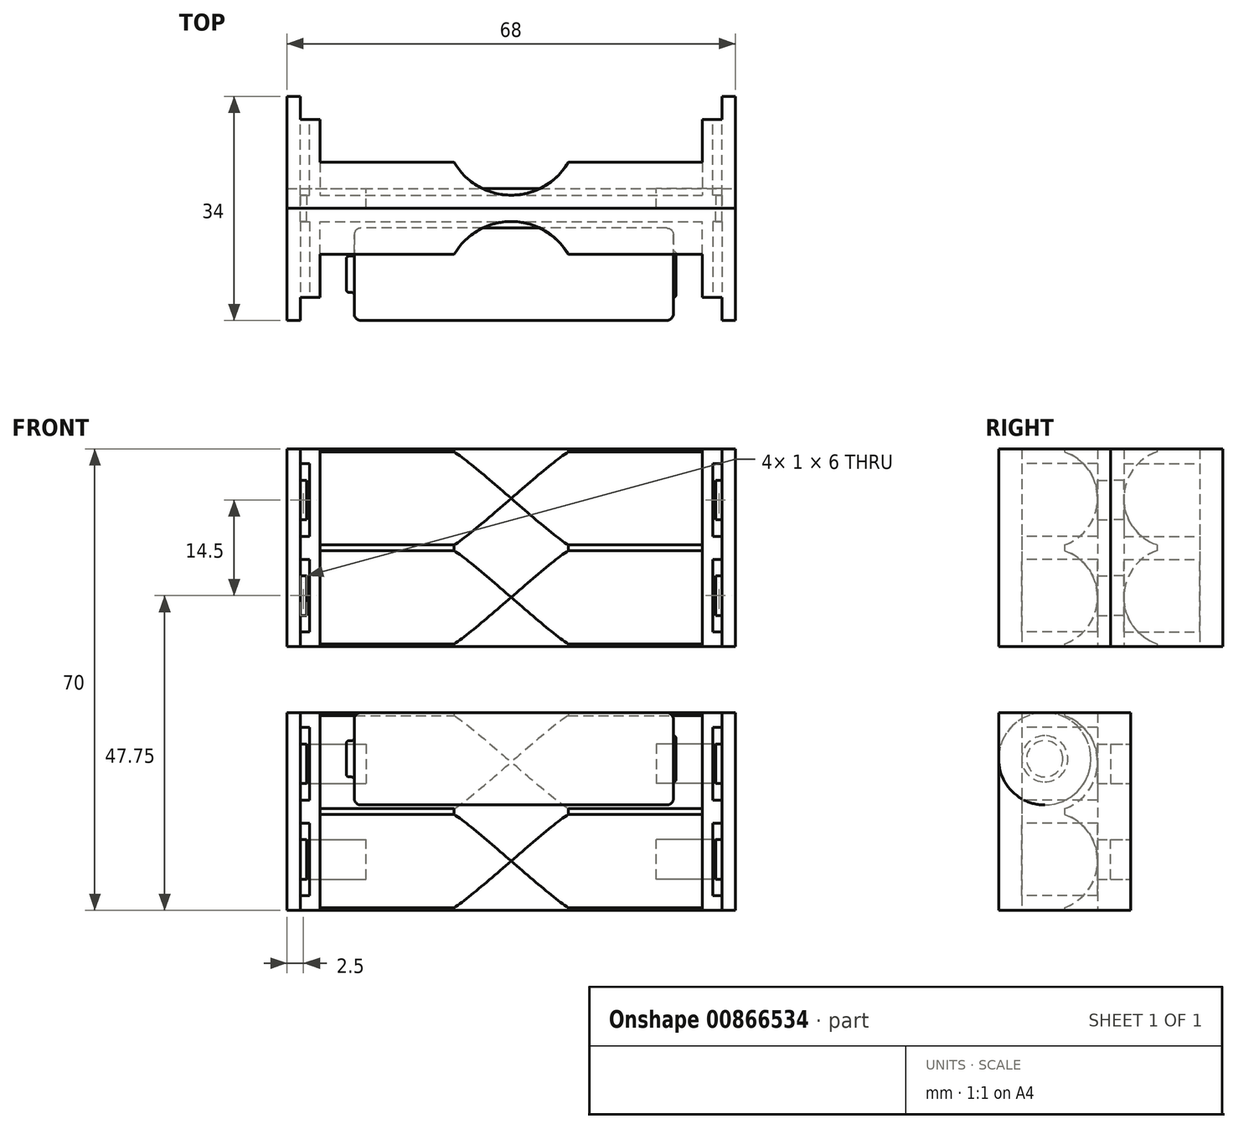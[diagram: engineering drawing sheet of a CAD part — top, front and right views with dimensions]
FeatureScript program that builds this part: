
annotation { "Feature Type Name" : "Feature", "Feature Type Description" : "" }
export const myFeature = defineFeature(function(context is Context, id is Id, definition is map)
    precondition{}
    {
        {
            var Q0;
            Q0=qCreatedBy(makeId("Top.planeOp"),FACE);
            var sketch = newSketch(context, id + "F0", { "sketchPlane" : qUnion([Q0])});
            skLineSegment(sketch, "E0.bottom", {"start": v(-34, 10) * mm, "end": v(34, 10) * mm});
            skLineSegment(sketch, "E0.top", {"start": v(-34, -10) * mm, "end": v(-32, -10) * mm});
            skLineSegment(sketch, "E0.left", {"start": v(-34, 10) * mm, "end": v(-34, -10) * mm});
            skLineSegment(sketch, "E0.right", {"start": v(34, 10) * mm, "end": v(34, -10) * mm});
            skLineSegment(sketch, "E1", {"start": v(0, 0) * mm, "end": v(0, 13.76) * mm, "construction": true});
            skArc(sketch, "E2", {"start": v(8.66, 0) * mm, "mid": v(0, 5) * mm, "end": v(-8.66, 0) * mm});
            skLineSegment(sketch, "E3", {"start": v(-32, -10) * mm, "end": v(-32, -6.5) * mm});
            skLineSegment(sketch, "E4", {"start": v(-32, -6.5) * mm, "end": v(-29, -6.5) * mm});
            skLineSegment(sketch, "E5", {"start": v(-29, -6.5) * mm, "end": v(-29, 0) * mm});
            skLineSegment(sketch, "E6", {"start": v(-29, 0) * mm, "end": v(-8.66, 0) * mm});
            skLineSegment(sketch, "E7", {"start": v(29, 0) * mm, "end": v(29, -6.5) * mm});
            skLineSegment(sketch, "E8", {"start": v(29, -6.5) * mm, "end": v(32, -6.5) * mm});
            skLineSegment(sketch, "E9", {"start": v(32, -6.5) * mm, "end": v(32, -10) * mm});
            skLineSegment(sketch, "E10.trimOffspring", {"start": v(32, -10) * mm, "end": v(34, -10) * mm});
            skLineSegment(sketch, "E11.trimOffspring", {"start": v(8.66, 0) * mm, "end": v(29, 0) * mm});
            skSolve(sketch);
        }
        {
            var Q0;
            Q0 = qSketchRegion(id + "F0", true);
            extrude(context, id + "F1", {"entities" : qUnion([Q0]), "endBound" : BoundingType.SYMMETRIC, "depth" : 30 * mm, "offsetDistance" : 25 * mm});
        }
        {
            var Q0;
            Q0=makeQuery(id+"F1.opExtrude","SWEPT_FACE",FACE,{"disambiguationData":[OSD([sQuery(id+"F0.wireOp",EDGE,"E4")])]});
            var sketch = newSketch(context, id + "F2", { "sketchPlane" : qUnion([Q0])});
            skLineSegment(sketch, "E12", {"start": v(0, 0) * mm, "end": v(0, 23.5) * mm, "construction": true});
            skLineSegment(sketch, "E13", {"start": v(0, 0) * mm, "end": v(-46.73, 0) * mm, "construction": true});
            skLineSegment(sketch, "E14.bottom", {"start": v(-32, 12.75) * mm, "end": v(-30.6, 12.75) * mm});
            skLineSegment(sketch, "E14.top", {"start": v(-32, 1.75) * mm, "end": v(-30.6, 1.75) * mm});
            skLineSegment(sketch, "E14.left", {"start": v(-32, 12.75) * mm, "end": v(-32, 1.75) * mm});
            skLineSegment(sketch, "E14.right", {"start": v(-30.6, 12.75) * mm, "end": v(-30.6, 1.75) * mm});
            skPoint(sketch, "E15", {"position": v(-30.6, 7.25) * mm});
            skLineSegment(sketch, "E16.MirrorCS", {"start": v(-32, -12.75) * mm, "end": v(-32, -1.75) * mm});
            skLineSegment(sketch, "E17.MirrorCS", {"start": v(-32, -12.75) * mm, "end": v(-30.6, -12.75) * mm});
            skLineSegment(sketch, "E18.MirrorCS", {"start": v(-30.6, -12.75) * mm, "end": v(-30.6, -1.75) * mm});
            skLineSegment(sketch, "E19.MirrorCS", {"start": v(-32, -1.75) * mm, "end": v(-30.6, -1.75) * mm});
            skLineSegment(sketch, "E20.MirrorCS", {"start": v(32, -1.75) * mm, "end": v(30.6, -1.75) * mm});
            skLineSegment(sketch, "E21.MirrorCS", {"start": v(32, 12.75) * mm, "end": v(30.6, 12.75) * mm});
            skLineSegment(sketch, "E22.MirrorCS", {"start": v(32, 1.75) * mm, "end": v(30.6, 1.75) * mm});
            skLineSegment(sketch, "E23.MirrorCS", {"start": v(32, -12.75) * mm, "end": v(30.6, -12.75) * mm});
            skLineSegment(sketch, "E24.MirrorCS", {"start": v(30.6, 12.75) * mm, "end": v(30.6, 1.75) * mm});
            skPoint(sketch, "E25.MirrorP", {"position": v(30.6, 7.25) * mm});
            skLineSegment(sketch, "E26.MirrorCS", {"start": v(32, 12.75) * mm, "end": v(32, 1.75) * mm});
            skLineSegment(sketch, "E27.MirrorCS", {"start": v(30.6, -12.75) * mm, "end": v(30.6, -1.75) * mm});
            skLineSegment(sketch, "E28.MirrorCS", {"start": v(32, -12.75) * mm, "end": v(32, -1.75) * mm});
            skSolve(sketch);
        }
        {
            var Q0;
            Q0 = qSketchRegion(id + "F2", true);
            extrude(context, id + "F3", {"entities" : qUnion([Q0]), "operationType" : NewBodyOperationType.REMOVE, "oppositeDirection" : true, "depth" : 11.5 * mm, "offsetDistance" : 25 * mm});
        }
        {
            var Q0;
            Q0=makeQuery(id+"F1.opExtrude","SWEPT_FACE",FACE,{"disambiguationData":[OSD([sQuery(id+"F0.wireOp",EDGE,"E0.bottom")])]});
            var sketch = newSketch(context, id + "F4", { "sketchPlane" : qUnion([Q0])});
            skLineSegment(sketch, "E29", {"start": v(0, 17.64) * mm, "end": v(0, 0) * mm, "construction": true});
            skLineSegment(sketch, "E30", {"start": v(0, 0) * mm, "end": v(-26.25, 0) * mm, "construction": true});
            skLineSegment(sketch, "E31.bottom", {"start": v(-32, 10.25) * mm, "end": v(-22, 10.25) * mm});
            skLineSegment(sketch, "E31.top", {"start": v(-32, 4.25) * mm, "end": v(-22, 4.25) * mm});
            skLineSegment(sketch, "E31.left", {"start": v(-32, 10.25) * mm, "end": v(-32, 4.25) * mm});
            skLineSegment(sketch, "E31.right", {"start": v(-22, 10.25) * mm, "end": v(-22, 4.25) * mm});
            skPoint(sketch, "E32", {"position": v(-22, 7.25) * mm});
            skLineSegment(sketch, "E33.MirrorCS", {"start": v(-22, -10.25) * mm, "end": v(-22, -4.25) * mm});
            skPoint(sketch, "E34.MirrorP", {"position": v(-22, -7.25) * mm});
            skLineSegment(sketch, "E35.MirrorCS", {"start": v(-32, -10.25) * mm, "end": v(-22, -10.25) * mm});
            skLineSegment(sketch, "E36.MirrorCS", {"start": v(-32, -4.25) * mm, "end": v(-22, -4.25) * mm});
            skLineSegment(sketch, "E37.MirrorCS", {"start": v(-32, -10.25) * mm, "end": v(-32, -4.25) * mm});
            skLineSegment(sketch, "E38.MirrorCS", {"start": v(22, -10.25) * mm, "end": v(22, -4.25) * mm});
            skLineSegment(sketch, "E39.MirrorCS", {"start": v(22, 10.25) * mm, "end": v(22, 4.25) * mm});
            skLineSegment(sketch, "E40.MirrorCS", {"start": v(32, 10.25) * mm, "end": v(32, 4.25) * mm});
            skPoint(sketch, "E41.MirrorP", {"position": v(22, -7.25) * mm});
            skPoint(sketch, "E42.MirrorP", {"position": v(22, 7.25) * mm});
            skLineSegment(sketch, "E43.MirrorCS", {"start": v(32, 10.25) * mm, "end": v(22, 10.25) * mm});
            skLineSegment(sketch, "E44.MirrorCS", {"start": v(32, -10.25) * mm, "end": v(22, -10.25) * mm});
            skLineSegment(sketch, "E45.MirrorCS", {"start": v(32, -10.25) * mm, "end": v(32, -4.25) * mm});
            skLineSegment(sketch, "E46.MirrorCS", {"start": v(32, 4.25) * mm, "end": v(22, 4.25) * mm});
            skLineSegment(sketch, "E47.MirrorCS", {"start": v(32, -4.25) * mm, "end": v(22, -4.25) * mm});
            skSolve(sketch);
        }
        {
            var Q0;
            Q0=makeQuery(id+"F1.opExtrude","SWEPT_FACE",FACE,{"disambiguationData":[OSD([sQuery(id+"F0.wireOp",EDGE,"E0.bottom")])]});
            var sketch = newSketch(context, id + "F5", { "sketchPlane" : qUnion([Q0])});
            skLineSegment(sketch, "E48.bottom", {"start": v(-32, 10.25) * mm, "end": v(-31, 10.25) * mm});
            skLineSegment(sketch, "E48.top", {"start": v(-32, 4.25) * mm, "end": v(-31, 4.25) * mm});
            skLineSegment(sketch, "E48.left", {"start": v(-32, 10.25) * mm, "end": v(-32, 4.25) * mm});
            skLineSegment(sketch, "E48.right", {"start": v(-31, 10.25) * mm, "end": v(-31, 4.25) * mm});
            skLineSegment(sketch, "E49", {"start": v(0, 3.67) * mm, "end": v(0, 0) * mm, "construction": true});
            skLineSegment(sketch, "E50", {"start": v(0, 0) * mm, "end": v(-16.48, 0) * mm, "construction": true});
            skPoint(sketch, "E51", {"position": v(-31, 7.25) * mm});
            skLineSegment(sketch, "E52.MirrorCS", {"start": v(-32, -10.25) * mm, "end": v(-31, -10.25) * mm});
            skLineSegment(sketch, "E53.MirrorCS", {"start": v(-32, -4.25) * mm, "end": v(-31, -4.25) * mm});
            skLineSegment(sketch, "E54.MirrorCS", {"start": v(-31, -10.25) * mm, "end": v(-31, -4.25) * mm});
            skLineSegment(sketch, "E55.MirrorCS", {"start": v(-32, -10.25) * mm, "end": v(-32, -4.25) * mm});
            skPoint(sketch, "E56.MirrorP", {"position": v(-31, -7.25) * mm});
            skLineSegment(sketch, "E57.MirrorCS", {"start": v(32, 10.25) * mm, "end": v(31, 10.25) * mm});
            skLineSegment(sketch, "E58.MirrorCS", {"start": v(32, -10.25) * mm, "end": v(31, -10.25) * mm});
            skLineSegment(sketch, "E59.MirrorCS", {"start": v(32, 4.25) * mm, "end": v(31, 4.25) * mm});
            skLineSegment(sketch, "E60.MirrorCS", {"start": v(32, -4.25) * mm, "end": v(31, -4.25) * mm});
            skPoint(sketch, "E61.MirrorP", {"position": v(31, -7.25) * mm});
            skLineSegment(sketch, "E62.MirrorCS", {"start": v(32, -10.25) * mm, "end": v(32, -4.25) * mm});
            skLineSegment(sketch, "E63.MirrorCS", {"start": v(32, 10.25) * mm, "end": v(32, 4.25) * mm});
            skLineSegment(sketch, "E64.MirrorCS", {"start": v(31, 10.25) * mm, "end": v(31, 4.25) * mm});
            skPoint(sketch, "E65.MirrorP", {"position": v(31, 7.25) * mm});
            skLineSegment(sketch, "E66.MirrorCS", {"start": v(31, -10.25) * mm, "end": v(31, -4.25) * mm});
            skSolve(sketch);
        }
        {
            var Q0;
            Q0 = qSketchRegion(id + "F4", true);
            extrude(context, id + "F6", {"entities" : qUnion([Q0]), "operationType" : NewBodyOperationType.REMOVE, "oppositeDirection" : true, "depth" : 3 * mm, "offsetDistance" : 25 * mm});
        }
        {
            var Q0;
            Q0 = qSketchRegion(id + "F5", true);
            extrude(context, id + "F7", {"entities" : qUnion([Q0]), "operationType" : NewBodyOperationType.REMOVE, "endBound" : BoundingType.THROUGH_ALL, "oppositeDirection" : true, "depth" : 25 * mm, "offsetDistance" : 25 * mm});
        }
        {
            var Q0;
            Q0=qCreatedBy(makeId("Right.planeOp"),FACE);
            var sketch = newSketch(context, id + "F8", { "sketchPlane" : qUnion([Q0])});
            skCircle(sketch, "E67", {"center": v(-2.5, 7.5) * mm, "radius": 7.5 * mm});
            skCircle(sketch, "E68", {"center": v(-2.5, -7.5) * mm, "radius": 7.5 * mm});
            skLineSegment(sketch, "E69", {"start": v(-2.5, 7.5) * mm, "end": v(-2.5, -7.5) * mm, "construction": true});
            skLineSegment(sketch, "E70", {"start": v(0, 0) * mm, "end": v(-2.5, 0) * mm, "construction": true});
            skSolve(sketch);
        }
        {
            var Q0;
            Q0 = qSketchRegion(id + "F8", true);
            extrude(context, id + "F9", {"entities" : qUnion([Q0]), "operationType" : NewBodyOperationType.REMOVE, "endBound" : BoundingType.SYMMETRIC, "oppositeDirection" : true, "depth" : 58 * mm, "offsetDistance" : 25 * mm});
        }
        {
            var Q0;
            Q0=qCreatedBy(makeId("Front.planeOp"),FACE);
            cPlane(context, id + "F10", {"entities" : qUnion([Q0]), "cplaneType" : CPlaneType.OFFSET, "offset" : 3 * mm, "width" : 150 * mm, "height" : 150 * mm});
        }
        {
            var Q0;
            Q0=qCreatedBy(id+"F10.planeOp",FACE);
            var sketch = newSketch(context, id + "F11", { "sketchPlane" : qUnion([Q0])});
            skLineSegment(sketch, "E71", {"start": v(-25, 8) * mm, "end": v(25, 8) * mm});
            skLineSegment(sketch, "E72", {"start": v(0, 0) * mm, "end": v(0, 17.32) * mm, "construction": true});
            skLineSegment(sketch, "E73", {"start": v(-25, 8) * mm, "end": v(-25, 5.25) * mm});
            skLineSegment(sketch, "E74", {"start": v(-25, 5.25) * mm, "end": v(-23.8, 5.25) * mm});
            skLineSegment(sketch, "E75", {"start": v(-23.8, 5.25) * mm, "end": v(-23.8, 1) * mm});
            skLineSegment(sketch, "E76", {"start": v(-23.8, 1) * mm, "end": v(24.6, 1) * mm});
            skLineSegment(sketch, "E77", {"start": v(24.6, 1) * mm, "end": v(24.6, 4.5) * mm});
            skLineSegment(sketch, "E78", {"start": v(24.6, 4.5) * mm, "end": v(25, 4.5) * mm});
            skLineSegment(sketch, "E79", {"start": v(25, 4.5) * mm, "end": v(25, 8) * mm});
            skLineSegment(sketch, "E80", {"start": v(25, 8) * mm, "end": v(27.91, 8) * mm, "construction": true});
            skSolve(sketch);
        }
        {
            var Q0;
            Q0=makeQuery(id+"F11.imprint","IMPRINT",FACE,{"disambiguationData":[TD([[makeQuery(id+"F11.imprint","IMPRINT",EDGE,{"derivedFrom":sQuery(id+"F11.wireOp",EDGE,"E71")}),-1.0]])]});
            var Q1;
            Q1=sQuery(id+"F11.wireOp",EDGE,"E80");
            revolve(context, id + "F12", {"surfaceOperationType" : NewSurfaceOperationType.NEW, "entities" : qUnion([Q0]), "axis" : qUnion([Q1]), "revolveType" : RevolveType.FULL});
        }
        {
            var Q0;
            Q0=makeQuery(id+"F12.opRevolve","SWEPT_EDGE",EDGE,{"disambiguationData":[OSD([sQuery(id+"F11.wireOp",EDGE,"E76"),sQuery(id+"F11.wireOp",EDGE,"E77")])]});
            var Q1;
            Q1=makeQuery(id+"F12.opRevolve","SWEPT_EDGE",EDGE,{"disambiguationData":[OSD([sQuery(id+"F11.wireOp",EDGE,"E75"),sQuery(id+"F11.wireOp",EDGE,"E76")])]});
            fillet(context, id + "F13", {"entities" : qUnion([Q0, Q1]), "radius" : 1 * mm, "tangentPropagation" : true, "allowEdgeOverflow" : false});
        }
        {
            var Q0;
            Q0=makeQuery(id+"F12.opRevolve","SWEPT_EDGE",EDGE,{"disambiguationData":[OSD([sQuery(id+"F11.wireOp",EDGE,"E78"),sQuery(id+"F11.wireOp",EDGE,"E79")])]});
            var Q1;
            Q1=makeQuery(id+"F12.opRevolve","SWEPT_EDGE",EDGE,{"disambiguationData":[OSD([sQuery(id+"F11.wireOp",EDGE,"E73"),sQuery(id+"F11.wireOp",EDGE,"E74")])]});
            var Q2;
            Q2=makeQuery(id+"F12.opRevolve","SWEPT_FACE",FACE,{"disambiguationData":[OSD([sQuery(id+"F11.wireOp",EDGE,"E75")])]});
            fillet(context, id + "F14", {"entities" : qUnion([Q0, Q1, Q2]), "radius" : 0.4 * mm, "tangentPropagation" : true, "allowEdgeOverflow" : false});
        }
        {
            var Q0;
            Q0=qCreatedBy(makeId("Front.planeOp"),FACE);
            cPlane(context, id + "F15", {"entities" : qUnion([Q0]), "cplaneType" : CPlaneType.OFFSET, "offset" : 7 * mm, "oppositeDirection" : true, "width" : 150 * mm, "height" : 150 * mm});
        }
        {
            var Q0;
            Q0=makeQuery(id+"F1.opExtrude","SWEPT_BODY",BODY,{"disambiguationData":[OSD([sQuery(id+"F0.wireOp",EDGE,"E0.bottom"),sQuery(id+"F0.wireOp",EDGE,"E0.top"),sQuery(id+"F0.wireOp",EDGE,"E0.left"),sQuery(id+"F0.wireOp",EDGE,"E0.right"),sQuery(id+"F0.wireOp",EDGE,"E2"),sQuery(id+"F0.wireOp",EDGE,"E3"),sQuery(id+"F0.wireOp",EDGE,"E4"),sQuery(id+"F0.wireOp",EDGE,"E5"),sQuery(id+"F0.wireOp",EDGE,"E6"),sQuery(id+"F0.wireOp",EDGE,"E7"),sQuery(id+"F0.wireOp",EDGE,"E8"),sQuery(id+"F0.wireOp",EDGE,"E9"),sQuery(id+"F0.wireOp",EDGE,"E10.trimOffspring"),sQuery(id+"F0.wireOp",EDGE,"E11.trimOffspring")])]});
            transform(context, id + "F16", {"entities" : qUnion([Q0]), "transformType" : TransformType.TRANSLATION_3D, "dx" : 0 * mm, "dy" : 0 * mm, "dz" : 40 * mm, "makeCopy" : true});
        }
        {
            var Q0;
            Q0=makeQuery(id+"F16.opPattern","COPY",FACE,{"derivedFrom":makeQuery(id+"F1.opExtrude","SWEPT_FACE",FACE,{"disambiguationData":[OSD([sQuery(id+"F0.wireOp",EDGE,"E0.bottom")])]}),"instanceName":"1"});
            var Q1;
            Q1=qCreatedBy(id+"F15.planeOp",FACE);
            extrude(context, id + "F17", {"entities" : qUnion([Q0]), "operationType" : NewBodyOperationType.REMOVE, "endBound" : BoundingType.UP_TO_SURFACE, "oppositeDirection" : true, "depth" : 3 * mm, "endBoundEntityFace" : qUnion([Q1]), "offsetDistance" : 25 * mm});
        }
        {
            var Q0;
            Q0=makeQuery(id+"F16.opPattern","COPY",BODY,{"derivedFrom":makeQuery(id+"F1.opExtrude","SWEPT_BODY",BODY,{"disambiguationData":[OSD([sQuery(id+"F0.wireOp",EDGE,"E0.bottom"),sQuery(id+"F0.wireOp",EDGE,"E0.top"),sQuery(id+"F0.wireOp",EDGE,"E0.left"),sQuery(id+"F0.wireOp",EDGE,"E0.right"),sQuery(id+"F0.wireOp",EDGE,"E2"),sQuery(id+"F0.wireOp",EDGE,"E3"),sQuery(id+"F0.wireOp",EDGE,"E4"),sQuery(id+"F0.wireOp",EDGE,"E5"),sQuery(id+"F0.wireOp",EDGE,"E6"),sQuery(id+"F0.wireOp",EDGE,"E7"),sQuery(id+"F0.wireOp",EDGE,"E8"),sQuery(id+"F0.wireOp",EDGE,"E9"),sQuery(id+"F0.wireOp",EDGE,"E10.trimOffspring"),sQuery(id+"F0.wireOp",EDGE,"E11.trimOffspring")])]}),"instanceName":"1"});
            var Q1;
            Q1=qCreatedBy(id+"F15.planeOp",FACE);
            mirror(context, id + "F18", {"operationType" : NewBodyOperationType.ADD, "entities" : qUnion([Q0]), "mirrorPlane" : qUnion([Q1])});
        }
    });
